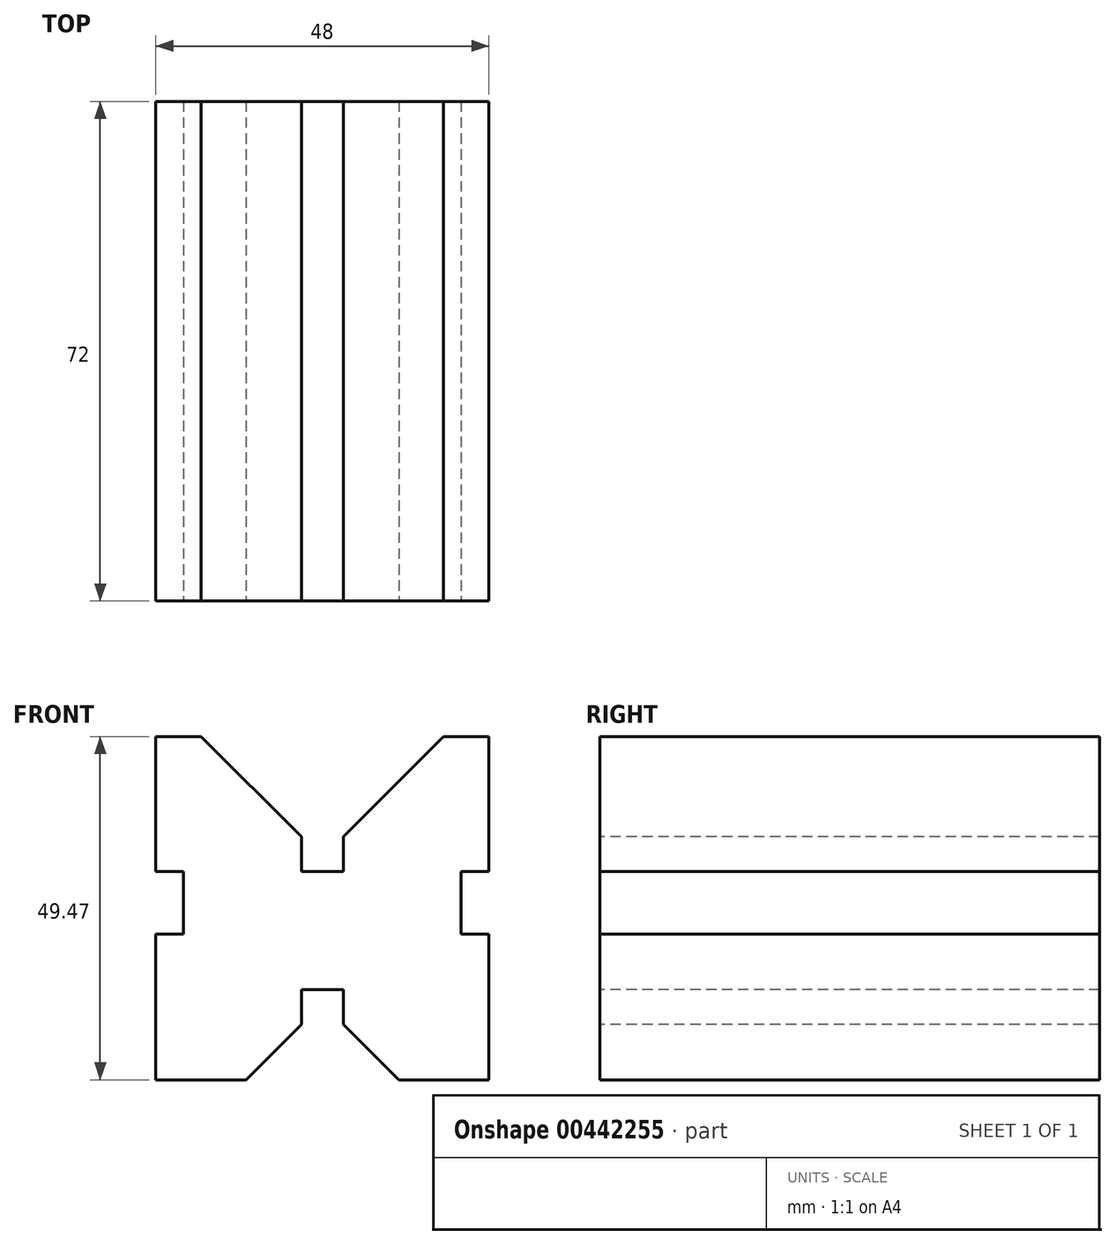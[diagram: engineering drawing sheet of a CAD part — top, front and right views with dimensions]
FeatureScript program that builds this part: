
annotation { "Feature Type Name" : "Feature", "Feature Type Description" : "" }
export const myFeature = defineFeature(function(context is Context, id is Id, definition is map)
    precondition{}
    {
        {
            var Q0;
            Q0=qCreatedBy(makeId("Front.planeOp"),FACE);
            var sketch = newSketch(context, id + "F0", { "sketchPlane" : qUnion([Q0])});
            skLineSegment(sketch, "E0.bottom", {"start": v(-24, 0) * mm, "end": v(-11, 0) * mm});
            skLineSegment(sketch, "E0.top", {"start": v(-24, 49.47) * mm, "end": v(-17.47, 49.47) * mm});
            skLineSegment(sketch, "E0.left", {"start": v(-24, 0) * mm, "end": v(-24, 21) * mm});
            skLineSegment(sketch, "E1.left", {"start": v(-3, 35) * mm, "end": v(-3, 30) * mm});
            skLineSegment(sketch, "E1.right", {"start": v(3, 35) * mm, "end": v(3, 30) * mm});
            skLineSegment(sketch, "E2.top", {"start": v(-3, 13) * mm, "end": v(3, 13) * mm});
            skLineSegment(sketch, "E2.left", {"start": v(-3, 8) * mm, "end": v(-3, 13) * mm});
            skLineSegment(sketch, "E2.right", {"start": v(3, 8) * mm, "end": v(3, 13) * mm});
            skPoint(sketch, "E3.firstSnap0", {"position": v(-24, 24.73) * mm});
            skLineSegment(sketch, "E3.bottom", {"start": v(-24, 30) * mm, "end": v(-20, 30) * mm});
            skLineSegment(sketch, "E3.top", {"start": v(-24, 21) * mm, "end": v(-20, 21) * mm});
            skLineSegment(sketch, "E3.right", {"start": v(-20, 30) * mm, "end": v(-20, 21) * mm});
            skLineSegment(sketch, "E4.bottom", {"start": v(24, 30) * mm, "end": v(20, 30) * mm});
            skLineSegment(sketch, "E4.top", {"start": v(24, 21) * mm, "end": v(20, 21) * mm});
            skLineSegment(sketch, "E4.right", {"start": v(20, 30) * mm, "end": v(20, 21) * mm});
            skLineSegment(sketch, "E5", {"start": v(0, 64.99) * mm, "end": v(0, -17.38) * mm, "construction": true});
            skPoint(sketch, "E6.orphan", {"position": v(0, 30) * mm});
            skPoint(sketch, "E7.orphan", {"position": v(0, 13) * mm});
            skLineSegment(sketch, "E8", {"start": v(-11, 0) * mm, "end": v(-3, 8) * mm});
            skLineSegment(sketch, "E9", {"start": v(3, 8) * mm, "end": v(11, 0) * mm});
            skLineSegment(sketch, "E10", {"start": v(-35.4, 24.73) * mm, "end": v(36.36, 24.73) * mm, "construction": true});
            skLineSegment(sketch, "E11.trimOffspring", {"start": v(11, 0) * mm, "end": v(24, 0) * mm});
            skPoint(sketch, "E12.orphan", {"position": v(-3, 0) * mm});
            skLineSegment(sketch, "E13.trimOffspring", {"start": v(-24, 30) * mm, "end": v(-24, 49.47) * mm});
            skLineSegment(sketch, "E14.trimOffspring", {"start": v(24, 30) * mm, "end": v(24, 49.47) * mm});
            skLineSegment(sketch, "E15", {"start": v(24, 0) * mm, "end": v(24, 21) * mm});
            skLineSegment(sketch, "E16.MirrorCS", {"start": v(24, 49.47) * mm, "end": v(17.47, 49.47) * mm});
            skLineSegment(sketch, "E17", {"start": v(-17.47, 49.47) * mm, "end": v(-3, 35) * mm});
            skLineSegment(sketch, "E18", {"start": v(3, 35) * mm, "end": v(17.47, 49.47) * mm});
            skLineSegment(sketch, "E19", {"start": v(-3, 30) * mm, "end": v(3, 30) * mm});
            skSolve(sketch);
        }
        {
            var Q0;
            Q0=makeQuery(id+"F0.imprint","IMPRINT",FACE,{"disambiguationData":[TD([[makeQuery(id+"F0.imprint","IMPRINT",EDGE,{"derivedFrom":sQuery(id+"F0.wireOp",EDGE,"E0.bottom")}),1.0]])]});
            extrude(context, id + "F1", {"entities" : qUnion([Q0]), "oppositeDirection" : true, "depth" : 72 * mm});
        }
    });
